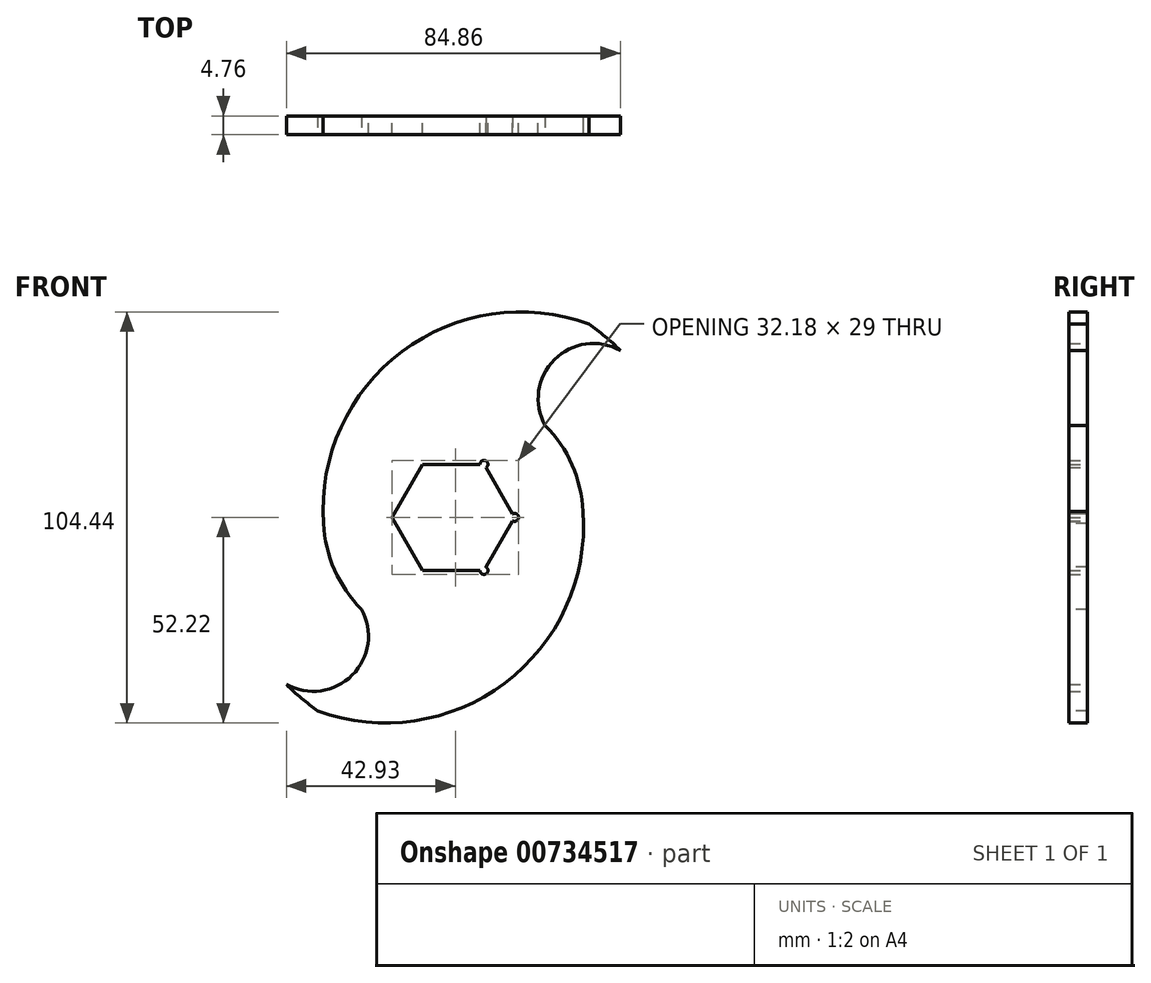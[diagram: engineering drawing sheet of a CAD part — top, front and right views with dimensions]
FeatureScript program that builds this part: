
annotation { "Feature Type Name" : "Feature", "Feature Type Description" : "" }
export const myFeature = defineFeature(function(context is Context, id is Id, definition is map)
    precondition{}
    {
        {
            var Q0;
            Q0=qCreatedBy(makeId("Front.planeOp"),FACE);
            var sketch = newSketch(context, id + "F0", { "sketchPlane" : qUnion([Q0])});
            skArc(sketch, "E0", {"start": v(-23.33, -23.33) * mm, "mid": v(-30.19, -13.33) * mm, "end": v(-32.97, -1.52) * mm});
            skArc(sketch, "E1", {"start": v(-32.97, -1.52) * mm, "mid": v(-13.05, 42.14) * mm, "end": v(34.43, 49.14) * mm});
            skArc(sketch, "E2", {"start": v(34.43, 49.14) * mm, "mid": v(38.57, 45.96) * mm, "end": v(42.43, 42.43) * mm});
            skArc(sketch, "E3", {"start": v(42.43, 42.43) * mm, "mid": v(25.68, 40.08) * mm, "end": v(23.33, 23.33) * mm});
            skArc(sketch, "E4", {"start": v(23.33, 23.33) * mm, "mid": v(30.19, 13.33) * mm, "end": v(32.97, 1.52) * mm});
            skArc(sketch, "E5", {"start": v(32.97, 1.52) * mm, "mid": v(13.05, -42.14) * mm, "end": v(-34.43, -49.14) * mm});
            skArc(sketch, "E6", {"start": v(-34.43, -49.14) * mm, "mid": v(-38.57, -45.96) * mm, "end": v(-42.43, -42.43) * mm});
            skArc(sketch, "E7", {"start": v(-42.43, -42.43) * mm, "mid": v(-25.68, -40.08) * mm, "end": v(-23.33, -23.33) * mm});
            skArc(sketch, "E8", {"start": v(6.8, 13.5) * mm, "mid": v(8.3, 14.37) * mm, "end": v(8.3, 12.63) * mm});
            skLineSegment(sketch, "E9", {"start": v(8.3, 12.63) * mm, "end": v(15.09, 0.87) * mm});
            skArc(sketch, "E10", {"start": v(15.09, 0.87) * mm, "mid": v(16.59, 0) * mm, "end": v(15.09, -0.87) * mm});
            skLineSegment(sketch, "E11", {"start": v(15.09, -0.87) * mm, "end": v(8.3, -12.63) * mm});
            skArc(sketch, "E12", {"start": v(8.3, -12.63) * mm, "mid": v(8.3, -14.37) * mm, "end": v(6.8, -13.5) * mm});
            skLineSegment(sketch, "E13", {"start": v(6.8, -13.5) * mm, "end": v(-7.8, -13.5) * mm});
            skLineSegment(sketch, "E14", {"start": v(-7.8, -13.5) * mm, "end": v(-15.59, 0) * mm});
            skLineSegment(sketch, "E15", {"start": v(-15.59, 0) * mm, "end": v(-7.8, 13.5) * mm});
            skLineSegment(sketch, "E16", {"start": v(-7.8, 13.5) * mm, "end": v(6.8, 13.5) * mm});
            skSolve(sketch);
        }
        {
            var Q0;
            Q0 = qSketchRegion(id + "F0", true);
            extrude(context, id + "F1", {"entities" : qUnion([Q0]), "depth" : 4.76 * mm, "offsetDistance" : 25.4 * mm});
        }
    });
